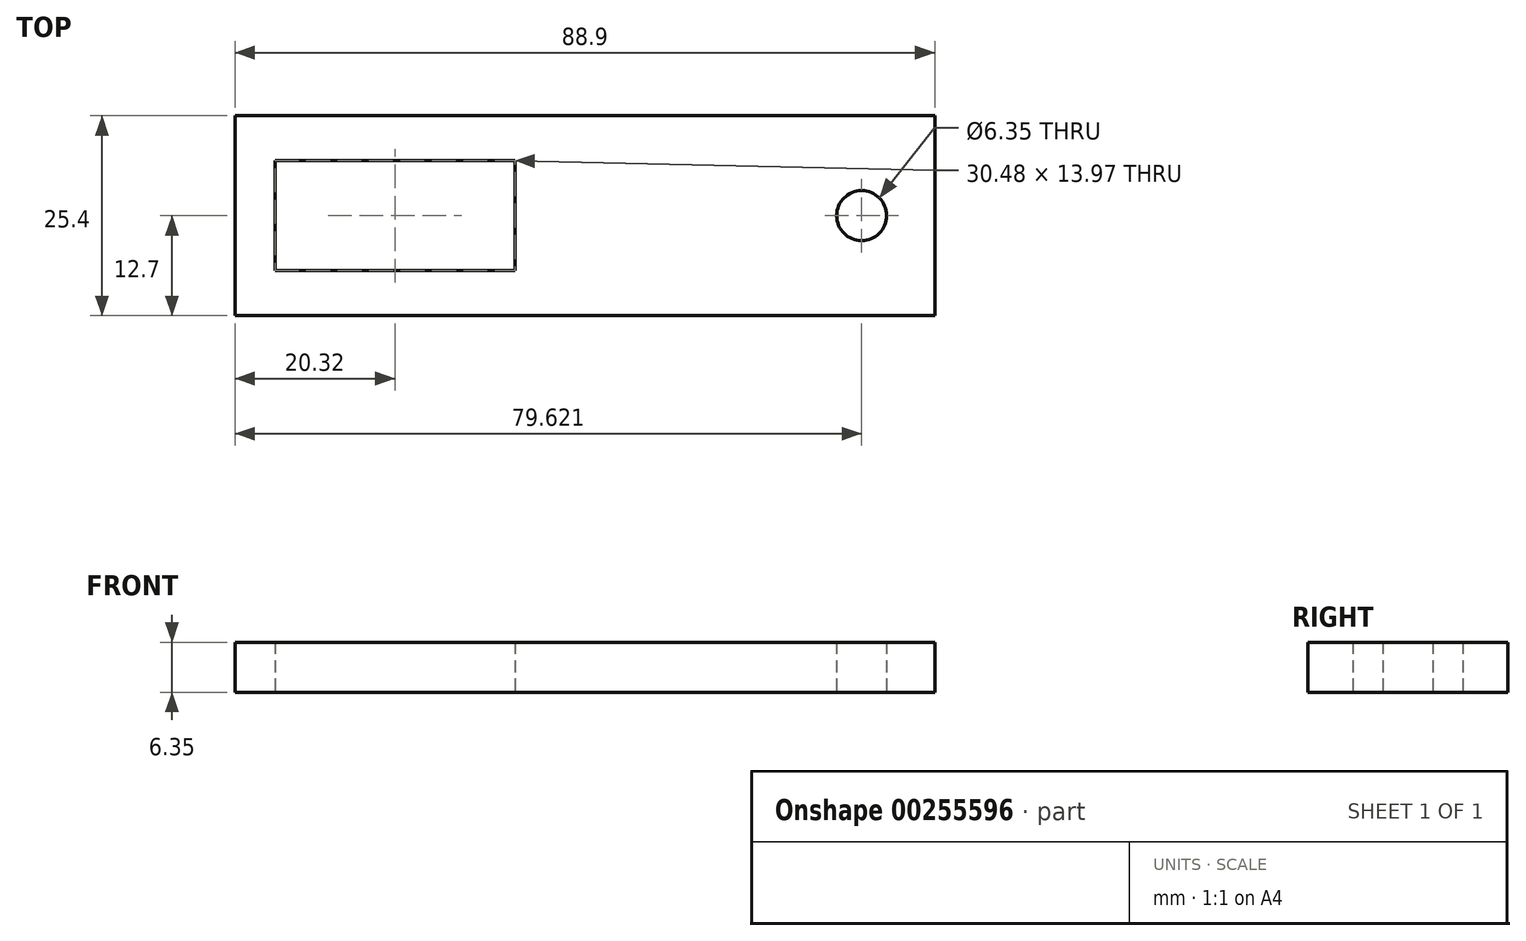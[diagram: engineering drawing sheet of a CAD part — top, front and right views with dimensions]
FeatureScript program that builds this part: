
annotation { "Feature Type Name" : "Feature", "Feature Type Description" : "" }
export const myFeature = defineFeature(function(context is Context, id is Id, definition is map)
    precondition{}
    {
        {
            var Q0;
            Q0=qCreatedBy(makeId("Top.planeOp"),FACE);
            var sketch = newSketch(context, id + "F0", { "sketchPlane" : qUnion([Q0])});
            skLineSegment(sketch, "E0.bottom", {"start": v(0, 0) * mm, "end": v(88.9, 0) * mm});
            skLineSegment(sketch, "E0.top", {"start": v(0, -25.4) * mm, "end": v(88.9, -25.4) * mm});
            skLineSegment(sketch, "E0.left", {"start": v(0, 0) * mm, "end": v(0, -25.4) * mm});
            skLineSegment(sketch, "E0.right", {"start": v(88.9, 0) * mm, "end": v(88.9, -25.4) * mm});
            skLineSegment(sketch, "E1.bottom", {"start": v(5.08, -5.71) * mm, "end": v(35.56, -5.71) * mm});
            skLineSegment(sketch, "E1.top", {"start": v(5.08, -19.69) * mm, "end": v(35.56, -19.69) * mm});
            skLineSegment(sketch, "E1.left", {"start": v(5.08, -5.71) * mm, "end": v(5.08, -19.69) * mm});
            skLineSegment(sketch, "E1.right", {"start": v(35.56, -5.71) * mm, "end": v(35.56, -19.69) * mm});
            skCircle(sketch, "E2", {"center": v(79.62, -12.7) * mm, "radius": 3.18 * mm});
            skSolve(sketch);
        }
        {
            var Q0;
            Q0=makeQuery(id+"F0.imprint","IMPRINT",FACE,{"disambiguationData":[TD([[makeQuery(id+"F0.imprint","IMPRINT",EDGE,{"derivedFrom":sQuery(id+"F0.wireOp",EDGE,"E0.bottom")}),-1.0]])]});
            extrude(context, id + "F1", {"entities" : qUnion([Q0]), "depth" : 6.35 * mm});
        }
    });
